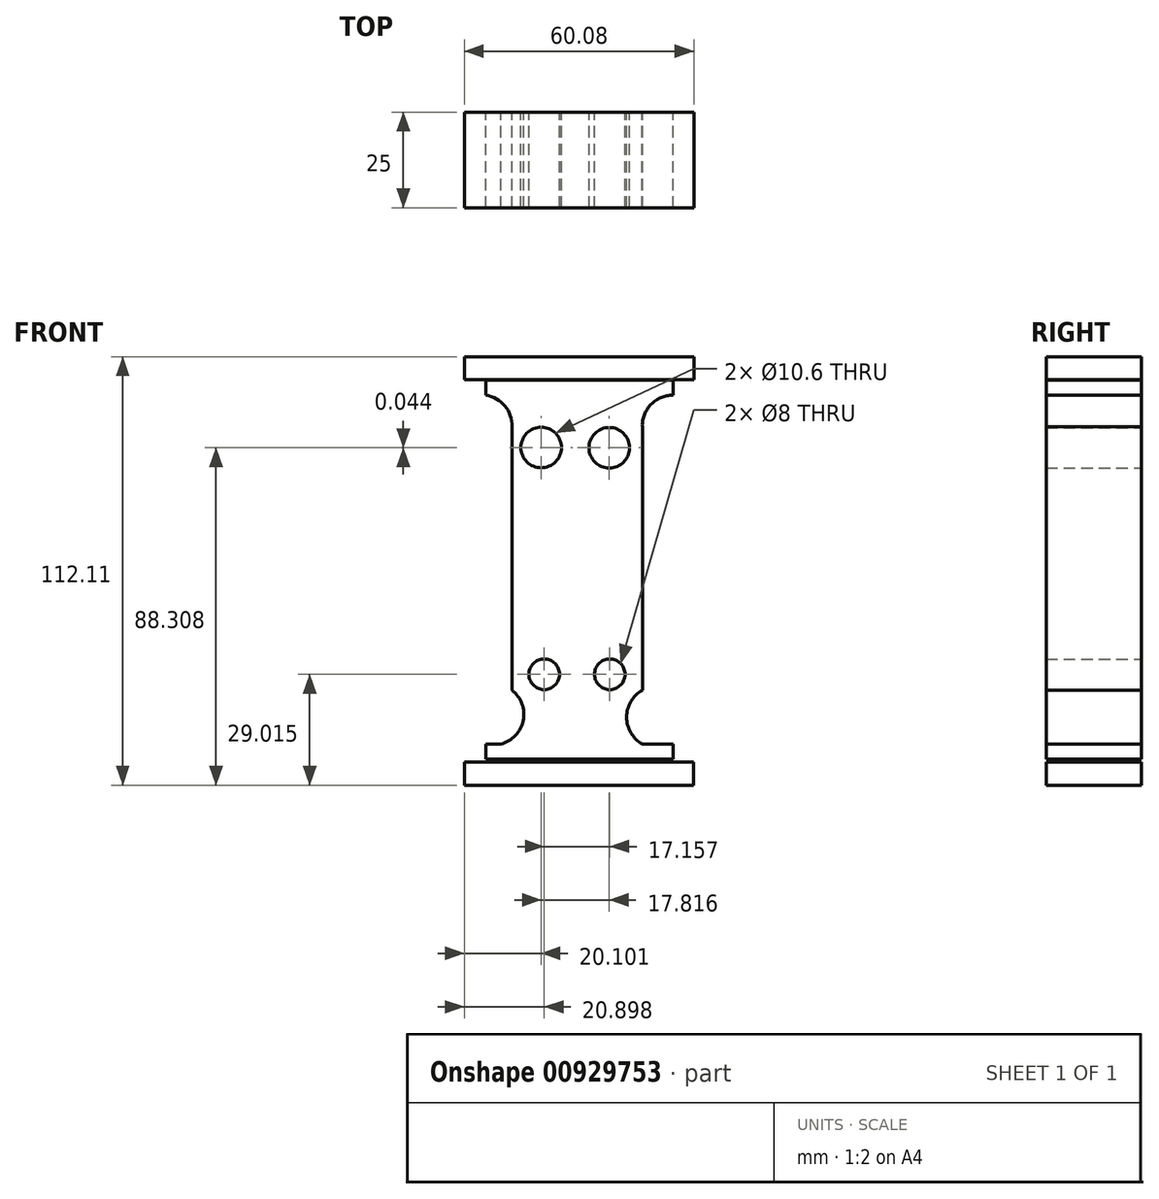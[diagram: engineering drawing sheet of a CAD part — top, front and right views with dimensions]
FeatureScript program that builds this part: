
annotation { "Feature Type Name" : "Feature", "Feature Type Description" : "" }
export const myFeature = defineFeature(function(context is Context, id is Id, definition is map)
    precondition{}
    {
        {
            var Q0;
            Q0=qCreatedBy(makeId("Front.planeOp"),FACE);
            var sketch = newSketch(context, id + "F0", { "sketchPlane" : qUnion([Q0])});
            skLineSegment(sketch, "E0.bottom", {"start": v(24.5, 44.14) * mm, "end": v(-24.5, 44.14) * mm});
            skLineSegment(sketch, "E0.top", {"start": v(24.5, 48.14) * mm, "end": v(-24.5, 48.14) * mm});
            skLineSegment(sketch, "E0.left", {"start": v(24.5, 44.14) * mm, "end": v(24.5, 48.14) * mm});
            skLineSegment(sketch, "E0.right", {"start": v(-24.5, 44.14) * mm, "end": v(-24.5, 48.14) * mm});
            skPoint(sketch, "E0.middle", {"position": v(0, 46.14) * mm});
            skLineSegment(sketch, "E1.bottom", {"start": v(30, 48.2) * mm, "end": v(-30, 48.2) * mm});
            skLineSegment(sketch, "E1.top", {"start": v(30, 54.2) * mm, "end": v(-30, 54.2) * mm});
            skLineSegment(sketch, "E1.left", {"start": v(30, 48.2) * mm, "end": v(30, 54.2) * mm});
            skLineSegment(sketch, "E1.right", {"start": v(-30, 48.2) * mm, "end": v(-30, 54.2) * mm});
            skPoint(sketch, "E1.middle", {"position": v(0, 51.2) * mm});
            skLineSegment(sketch, "E2.bottom", {"start": v(24.5, -51.14) * mm, "end": v(-24.5, -51.14) * mm});
            skLineSegment(sketch, "E2.top", {"start": v(24.5, -47.14) * mm, "end": v(-24.5, -47.14) * mm});
            skLineSegment(sketch, "E2.left", {"start": v(24.5, -51.14) * mm, "end": v(24.5, -47.14) * mm});
            skLineSegment(sketch, "E2.right", {"start": v(-24.5, -51.14) * mm, "end": v(-24.5, -47.14) * mm});
            skPoint(sketch, "E2.middle", {"position": v(0, -49.14) * mm});
            skLineSegment(sketch, "E3", {"start": v(-17.62, 35.94) * mm, "end": v(-17.62, -33.06) * mm});
            skLineSegment(sketch, "E4", {"start": v(16.5, 35.94) * mm, "end": v(16.5, -33.06) * mm});
            skLineSegment(sketch, "E5", {"start": v(-17.62, 35.94) * mm, "end": v(16.5, 35.94) * mm});
            skArc(sketch, "E6", {"start": v(-17.62, 35.94) * mm, "mid": v(-19.49, 41.36) * mm, "end": v(-24.5, 44.14) * mm});
            skArc(sketch, "E7", {"start": v(24.5, 44.14) * mm, "mid": v(18.77, 41.73) * mm, "end": v(16.5, 35.94) * mm});
            skLineSegment(sketch, "E8", {"start": v(-17.62, -33.06) * mm, "end": v(15.83, -33.06) * mm});
            skArc(sketch, "E9", {"start": v(-24.5, -47.14) * mm, "mid": v(-15.33, -42.9) * mm, "end": v(-17.62, -33.06) * mm});
            skArc(sketch, "E10", {"start": v(16.5, -33.06) * mm, "mid": v(13.46, -44.1) * mm, "end": v(24.5, -47.14) * mm});
            skLineSegment(sketch, "E11.bottom", {"start": v(29.92, -57.91) * mm, "end": v(-30.08, -57.91) * mm});
            skLineSegment(sketch, "E11.top", {"start": v(29.92, -51.91) * mm, "end": v(-30.08, -51.91) * mm});
            skLineSegment(sketch, "E11.left", {"start": v(29.92, -57.91) * mm, "end": v(29.92, -51.91) * mm});
            skLineSegment(sketch, "E11.right", {"start": v(-30.08, -57.91) * mm, "end": v(-30.08, -51.91) * mm});
            skPoint(sketch, "E11.middle", {"position": v(-0.08, -54.91) * mm});
            skCircle(sketch, "E12", {"center": v(7.84, 30.4) * mm, "radius": 5.3 * mm});
            skCircle(sketch, "E13", {"center": v(-9.98, 30.44) * mm, "radius": 5.3 * mm});
            skCircle(sketch, "E14", {"center": v(-9.18, -28.9) * mm, "radius": 4 * mm});
            skCircle(sketch, "E15", {"center": v(7.97, -28.9) * mm, "radius": 4 * mm});
            skSolve(sketch);
        }
        {
            var Q0;
            Q0=makeQuery(id+"F0.imprint","IMPRINT",FACE,{"disambiguationData":[TD([[makeQuery(id+"F0.imprint","IMPRINT",EDGE,{"derivedFrom":sQuery(id+"F0.wireOp",EDGE,"E11.bottom")}),-1.0]])]});
            var Q1;
            Q1=makeQuery(id+"F0.imprint","IMPRINT",FACE,{"disambiguationData":[TD([[makeQuery(id+"F0.imprint","IMPRINT",EDGE,{"derivedFrom":sQuery(id+"F0.wireOp",EDGE,"E1.bottom")}),-1.0]])]});
            var Q2;
            {var subQ1=sQuery(id+"F0.wireOp",EDGE,"E0.bottom");Q2=makeQuery(id+"F0.imprint","IMPRINT",FACE,{"disambiguationData":[TD([[makeQuery(id+"F0.imprint","IMPRINT",EDGE,{"derivedFrom":subQ1}),-1.0]])]});}
            var Q3;
            Q3=makeQuery(id+"F0.imprint","IMPRINT",FACE,{"disambiguationData":[TD([[makeQuery(id+"F0.imprint","IMPRINT",EDGE,{"derivedFrom":sQuery(id+"F0.wireOp",EDGE,"E2.bottom")}),-1.0]])]});
            var Q4;
            {var subQ0=sQuery(id+"F0.wireOp",EDGE,"E0.bottom");Q4=makeQuery(id+"F0.imprint","IMPRINT",FACE,{"disambiguationData":[TD([[makeQuery(id+"F0.imprint","IMPRINT",EDGE,{"derivedFrom":subQ0}),1.0]])]});}
            var Q5;
            {var subQ0=sQuery(id+"F0.wireOp",EDGE,"E9");var subQ1=sQuery(id+"F0.wireOp",EDGE,"E2.top");var subQ3=makeQuery(id+"F0.imprint","INTERSECT",VERTEX,{"derivedFrom":[subQ1,subQ0]});Q5=makeQuery(id+"F0.imprint","IMPRINT",FACE,{"disambiguationData":[TD([[makeQuery(id+"F0.imprint","IMPRINT",EDGE,{"disambiguationData":[TD([[subQ3,-1.0]])],"derivedFrom":subQ1}),1.0]])]});}
            var Q6;
            {var subQ0=sQuery(id+"F0.wireOp",EDGE,"E10");var subQ1=sQuery(id+"F0.wireOp",EDGE,"E2.top");var subQ3=makeQuery(id+"F0.imprint","INTERSECT",VERTEX,{"derivedFrom":[subQ1,subQ0]});Q6=makeQuery(id+"F0.imprint","IMPRINT",FACE,{"disambiguationData":[TD([[makeQuery(id+"F0.imprint","IMPRINT",EDGE,{"disambiguationData":[TD([[subQ3,1.0]])],"derivedFrom":subQ1}),1.0]])]});}
            var Q7;
            {var subQ0=sQuery(id+"F0.wireOp",EDGE,"E3");Q7=makeQuery(id+"F0.imprint","IMPRINT",FACE,{"disambiguationData":[TD([[makeQuery(id+"F0.imprint","IMPRINT",EDGE,{"derivedFrom":subQ0}),1.0]])]});}
            extrude(context, id + "F1", {"entities" : qUnion([Q0, Q1, Q2, Q3, Q4, Q5, Q6, Q7]), "depth" : 25 * mm, "offsetDistance" : 25 * mm});
        }
    });
